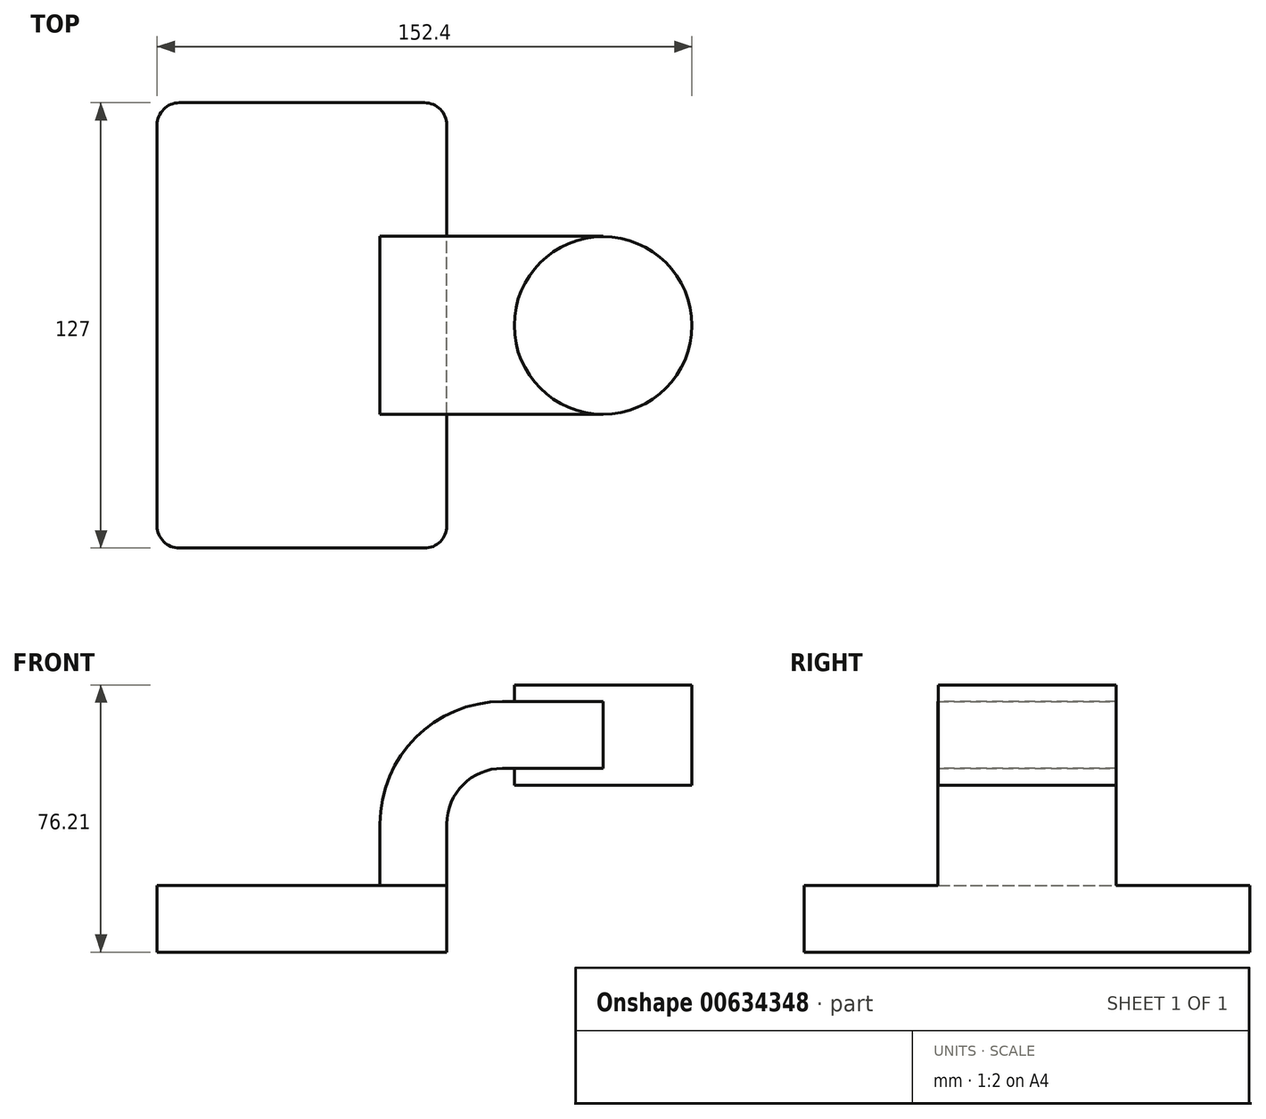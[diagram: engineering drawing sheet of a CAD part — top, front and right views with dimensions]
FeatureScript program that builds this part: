
annotation { "Feature Type Name" : "Feature", "Feature Type Description" : "" }
export const myFeature = defineFeature(function(context is Context, id is Id, definition is map)
    precondition{}
    {
        {
            var Q0;
            Q0=qCreatedBy(makeId("Front.planeOp"),FACE);
            var sketch = newSketch(context, id + "F0", { "sketchPlane" : qUnion([Q0])});
            skLineSegment(sketch, "E0.bottom", {"start": v(41.27, 9.53) * mm, "end": v(-41.28, 9.53) * mm});
            skLineSegment(sketch, "E0.top", {"start": v(41.28, -9.52) * mm, "end": v(-41.27, -9.52) * mm});
            skLineSegment(sketch, "E0.left", {"start": v(41.27, 9.53) * mm, "end": v(41.28, -9.52) * mm});
            skLineSegment(sketch, "E0.right", {"start": v(-41.28, 9.53) * mm, "end": v(-41.27, -9.52) * mm});
            skPoint(sketch, "E0.middle", {"position": v(0, 0) * mm});
            skLineSegment(sketch, "E1.bottom", {"start": v(60.33, 38.1) * mm, "end": v(111.12, 38.1) * mm});
            skLineSegment(sketch, "E1.top", {"start": v(60.32, 66.68) * mm, "end": v(111.12, 66.68) * mm});
            skLineSegment(sketch, "E1.left", {"start": v(60.33, 38.1) * mm, "end": v(60.32, 66.68) * mm});
            skLineSegment(sketch, "E1.right", {"start": v(111.13, 38.1) * mm, "end": v(111.13, 66.68) * mm});
            skPoint(sketch, "E1.middle", {"position": v(85.72, 52.39) * mm});
            skLineSegment(sketch, "E2", {"start": v(41.27, 9.53) * mm, "end": v(41.27, 27) * mm});
            skArc(sketch, "E3", {"start": v(41.27, 27) * mm, "mid": v(45.92, 38.23) * mm, "end": v(57.15, 42.88) * mm});
            skLineSegment(sketch, "E4", {"start": v(57.15, 42.88) * mm, "end": v(85.8, 42.88) * mm});
            skLineSegment(sketch, "E5.0", {"start": v(57.15, 61.93) * mm, "end": v(85.8, 61.93) * mm});
            skArc(sketch, "E5.1", {"start": v(22.22, 27) * mm, "mid": v(32.45, 51.7) * mm, "end": v(57.15, 61.93) * mm});
            skLineSegment(sketch, "E5.2", {"start": v(22.22, 9.53) * mm, "end": v(22.22, 27) * mm});
            skLineSegment(sketch, "E6", {"start": v(85.8, 66.68) * mm, "end": v(85.8, 38.1) * mm});
            skFitSpline(sketch, "E7", {"points": [v(-41.28, 9.52) * mm, v(57.15, 61.93) * mm], "startDerivative": vector(1.02, 77.64) * mm, "endDerivative": vector(122.34, -6.6) * mm});
            skSolve(sketch);
        }
        {
            var Q0;
            Q0=makeQuery(id+"F0.imprint","IMPRINT",FACE,{"disambiguationData":[TD([[makeQuery(id+"F0.imprint","IMPRINT",EDGE,{"derivedFrom":sQuery(id+"F0.wireOp",EDGE,"E0.top")}),-1.0]])]});
            extrude(context, id + "F1", {"entities" : qUnion([Q0]), "endBound" : BoundingType.SYMMETRIC, "depth" : 127 * mm, "offsetDistance" : 25.4 * mm});
        }
        {
            var Q0;
            {var subQ1=sQuery(id+"F0.wireOp",EDGE,"E2");Q0=makeQuery(id+"F0.imprint","IMPRINT",FACE,{"disambiguationData":[TD([[makeQuery(id+"F0.imprint","IMPRINT",EDGE,{"derivedFrom":subQ1}),1.0]])]});}
            var Q1;
            {var subQ0=sQuery(id+"F0.wireOp",EDGE,"E4");var subQ1=sQuery(id+"F0.wireOp",EDGE,"E1.left");var subQ2=makeQuery(id+"F0.imprint","INTERSECT",VERTEX,{"derivedFrom":[subQ1,subQ0]});Q1=makeQuery(id+"F0.imprint","IMPRINT",FACE,{"disambiguationData":[TD([[makeQuery(id+"F0.imprint","IMPRINT",EDGE,{"disambiguationData":[TD([[subQ2,-1.0]])],"derivedFrom":subQ1}),-1.0]])]});}
            extrude(context, id + "F2", {"entities" : qUnion([Q0, Q1]), "operationType" : NewBodyOperationType.ADD, "endBound" : BoundingType.SYMMETRIC, "depth" : 50.8 * mm, "offsetDistance" : 25.4 * mm});
        }
        {
            var Q0;
            Q0=makeQuery(id+"F0.imprint","IMPRINT",FACE,{"disambiguationData":[TD([[makeQuery(id+"F0.imprint","IMPRINT",EDGE,{"derivedFrom":sQuery(id+"F0.wireOp",EDGE,"E5.1")}),1.0]])]});
            extrude(context, id + "F3", {"entities" : qUnion([Q0]), "operationType" : NewBodyOperationType.ADD, "endBound" : BoundingType.SYMMETRIC, "depth" : 15.88 * mm, "offsetDistance" : 25.4 * mm});
        }
        {
            var Q0;
            {var subQ0=sQuery(id+"F0.wireOp",EDGE,"E1.right");Q0=makeQuery(id+"F0.imprint","IMPRINT",FACE,{"disambiguationData":[TD([[makeQuery(id+"F0.imprint","IMPRINT",EDGE,{"derivedFrom":subQ0}),1.0]])]});}
            var Q1;
            Q1=sQuery(id+"F0.wireOp",EDGE,"E6");
            revolve(context, id + "F4", {"operationType" : NewBodyOperationType.ADD, "entities" : qUnion([Q0]), "axis" : qUnion([Q1]), "revolveType" : RevolveType.FULL});
        }
        {
            var Q0;
            Q0=makeQuery(id+"F1.opExtrude","CAP_EDGE",EDGE,{"disambiguationData":[OSD([sQuery(id+"F0.wireOp",EDGE,"E0.left")])],"isStart":true});
            var Q1;
            Q1=makeQuery(id+"F1.opExtrude","CAP_EDGE",EDGE,{"disambiguationData":[OSD([sQuery(id+"F0.wireOp",EDGE,"E0.right")])],"isStart":true});
            var Q2;
            Q2=makeQuery(id+"F1.opExtrude","CAP_EDGE",EDGE,{"disambiguationData":[OSD([sQuery(id+"F0.wireOp",EDGE,"E0.right")])],"isStart":false});
            var Q3;
            Q3=makeQuery(id+"F1.opExtrude","CAP_EDGE",EDGE,{"disambiguationData":[OSD([sQuery(id+"F0.wireOp",EDGE,"E0.left")])],"isStart":false});
            fillet(context, id + "F5", {"entities" : qUnion([Q0, Q1, Q2, Q3]), "radius" : 6.35 * mm, "tangentPropagation" : true, "allowEdgeOverflow" : false});
        }
    });
